# Revit family: Zurn_Z1464_Control-Box
name_source: partatom
category: Plumbing Fixtures
units: mm (PartAtom-declared; Revit-internal decimal feet)

## family parameters
Cut with Voids When Loaded = No
Host = Face
Maintain Annotation Orientation = No
OmniClass Number = 23.65.70.00
OmniClass Title = Terminals for Supplied Liquids and Gases
Part Type = Normal
Room Calculation Point = No
Round Connector Dimension = Use Radius
Shared = No

## types (1)
- Z1464
    Approx. Weigth (Lbs) = 17.00 lb
    Assembly Code = D2030400
    CW Connection = Yes
    CWFU = 1
    Connector Radius = 0.5 "
    Control Box Depth = 4.875 "
    Control Box Height = 8.375 "
    Control Box Length = 9.625 "
    Control Box Opening Size (AxA) = 8.5 "
    Default Elevation = 20 "
    Description = WATER SUPPLY CONTROL BOX ASSEMBY
    Female Connections Length from back = 1.75 "
    Female Connections Size = 1 "
    HW Connection = Yes
    HWFU = 1
    Main Material = Steel - Zurn - Stainless - Type - 304
    Manufacturer = Zurn Industries, LLC
    Manufacturer Brand = Zurn
    Model = Z1464
    Modified Date = 01/30/2026
    Product Documentation Link = https://files.zurn.com
    Product Page URL = https://www.zurn.com
    Product data url = https://www.bimobject.com
    URL = www.zurn.com
    Vent Connection = No
    WFU = 0
    Waste Connection = No

## geometry (parser evidence)
native form markers: Sweep x4
no freeform markers — native parametric forms only
